# Revit family: 10_給気タイプ 消音形 単相100V_3相200V-60
name_source: partatom
category: 機械設備
units: mm (PartAtom-declared; Revit-internal decimal feet)

## family parameters
OmniClass タイトル = Centrifugal Fans
OmniClass 番号 = 23.75.35.17.27
パーツ タイプ = 割り込み
ロード時にボイドで切り取り = いいえ
丸型コネクタ寸法 = 直径を使用
作業面ベース = いいえ
共有 = いいえ
常に垂直 = はい
部屋計算ポイント = はい

## types (7) — shared parameters
Clearance Left = 450  [stored 1.47638 ft]
IfcExportAs = IfcFanType
IfcExportType = CENTRIFUGALFORWARDCURVED
MID静圧 = 0.0 Pa
MID風量 = 0.0 m³/h
OmniClassCode = 23-33 31 19 13 15
URL = https://www.mitsubishielectric.co.jp
Uniclass2015Code = Pr_65_67_29_12
Uniclass2015Title = Centrifugal fans
Uniclass2015Version = Systems v1.9
サービススペース = はい
ファンの種類 = 多翼形
仕様書バージョン = Version1.0
企業コード = 108420
分類コード = 50052502100020
参照している仕様書等のバージョン = 公共建築工事標準仕様書（機械設備工事編）平成31年度版
周波数 = 60 Hz
呼称 = 消音ボックス付送風機
実風量 = 0.0 m³/h
本体マテリアル = 溶融亜鉛めっき鋼板
極 = 4
法定耐用年数 = 15
盤工事区分 = 電気工事
積算_科目 = 2 換気設備
製品リリース年月 = 2020年4月27日
製品出荷対象 = 国内
製造元 = 三菱電機株式会社
設置方法 = 天吊
説明 = ストレートシロッコファン給気タイプ消音形
負荷分類 = 3_ファン類
運転質量 = 0.00 kg
zero-valued in all types: Clearance Back, Clearance Bottom, Clearance Front, Clearance Right, Clearance Top

## per-type parameters (varying)
- BFS-40SSUA: Depth=378  [stored 1.24016 ft]; Height=255  [stored 0.836614 ft]; M=70  [stored 0.229659 ft]; MAX静圧=97.0 Pa; MAX風量=400.0 m³/h; MIN静圧=41.0 Pa; MIN風量=204.0 m³/h; Width=282; ダクト径=150 mm; 価格=86900 $; 天吊金具ピッチ奥行=343  [stored 1.12533 ft]; 天吊金具ピッチ幅=358  [stored 1.17454 ft]; 形名=BFS-SSUA : BFS-40SSUA; 極数=2; 消費電力=85 W; 番手=#1 1/4; 相=1; 製品質量=10.50 kg; 質量=12.60 kg; 電動機出力=35 W; 電圧=100 V; 騒音レベル(dB(A))=42; 騒音レベル(dB(A))_側面=20.5; 騒音レベル(dB(A))_吐出=39; 騒音レベル(dB(A))_吸込=42
- BFS-50SSUA: Depth=423  [stored 1.3878 ft]; Height=255  [stored 0.836614 ft]; M=85  [stored 0.278871 ft]; MAX静圧=190.0 Pa; MAX風量=500.0 m³/h; MIN静圧=120.0 Pa; MIN風量=395.0 m³/h; Width=325  [stored 1.06627 ft]; ダクト径=200 mm; 価格=123000 $; 天吊金具ピッチ奥行=388  [stored 1.27297 ft]; 天吊金具ピッチ幅=401  [stored 1.31562 ft]; 形名=BFS-SSUA : BFS-50SSUA; 極数=2; 消費電力=100 W; 番手=#1 1/4; 相=1; 製品質量=12.50 kg; 質量=15.00 kg; 電動機出力=45 W; 電圧=100 V; 騒音レベル(dB(A))=45.5; 騒音レベル(dB(A))_側面=23.5; 騒音レベル(dB(A))_吐出=41; 騒音レベル(dB(A))_吸込=45.5
- BFS-80SSUA: Depth=463  [stored 1.51903 ft]; Height=305  [stored 1.00066 ft]; M=85  [stored 0.278871 ft]; MAX静圧=165.0 Pa; MAX風量=800.0 m³/h; MIN静圧=109.0 Pa; MIN風量=650.0 m³/h; Width=373  [stored 1.22375 ft]; ダクト径=200 mm; 価格=137000 $; 天吊金具ピッチ奥行=428  [stored 1.4042 ft]; 天吊金具ピッチ幅=449  [stored 1.4731 ft]; 形名=BFS-SSUA : BFS-80SSUA; 極数=2; 消費電力=210 W; 番手=#1 1/4; 相=1; 製品質量=16.00 kg; 質量=19.20 kg; 電動機出力=110 W; 電圧=100 V; 騒音レベル(dB(A))=51; 騒音レベル(dB(A))_側面=28; 騒音レベル(dB(A))_吐出=44.5; 騒音レベル(dB(A))_吸込=51
- BFS-100SSUA: Depth=488  [stored 1.60105 ft]; Height=305  [stored 1.00066 ft]; M=85  [stored 0.278871 ft]; MAX静圧=260.0 Pa; MAX風量=1000.0 m³/h; MIN静圧=215.0 Pa; MIN風量=880.0 m³/h; Width=393  [stored 1.28937 ft]; ダクト径=200 mm; 価格=154000 $; 天吊金具ピッチ奥行=453  [stored 1.48622 ft]; 天吊金具ピッチ幅=469; 形名=BFS-SSUA : BFS-100SSUA; 極数=2; 消費電力=280 W; 番手=#1 1/2; 相=1; 製品質量=18.00 kg; 質量=21.60 kg; 電動機出力=200 W; 電圧=100 V; 騒音レベル(dB(A))=53; 騒音レベル(dB(A))_側面=32; 騒音レベル(dB(A))_吐出=51; 騒音レベル(dB(A))_吸込=53
- BFS-150SSUA: Depth=590  [stored 1.9357 ft]; Height=350  [stored 1.14829 ft]; M=85  [stored 0.278871 ft]; MAX静圧=320.0 Pa; MAX風量=1500.0 m³/h; MIN静圧=230.0 Pa; MIN風量=1275.0 m³/h; Width=391; ダクト径=250 mm; 価格=176000 $; 天吊金具ピッチ奥行=555  [stored 1.82087 ft]; 天吊金具ピッチ幅=467  [stored 1.53215 ft]; 形名=BFS-SSUA : BFS-150SSUA; 極数=2; 消費電力=515 W; 番手=#1 1/2; 相=1; 製品質量=23.50 kg; 質量=28.20 kg; 電動機出力=300 W; 電圧=100 V; 騒音レベル(dB(A))=60.5; 騒音レベル(dB(A))_側面=35; 騒音レベル(dB(A))_吐出=56; 騒音レベル(dB(A))_吸込=60.5
- BFS-150STUA: Depth=590  [stored 1.9357 ft]; Height=350  [stored 1.14829 ft]; M=85  [stored 0.278871 ft]; MAX静圧=320.0 Pa; MAX風量=1500.0 m³/h; MIN静圧=175.0 Pa; MIN風量=1110.0 m³/h; Width=391; ダクト径=250 mm; 価格=176000 $; 天吊金具ピッチ奥行=555  [stored 1.82087 ft]; 天吊金具ピッチ幅=467  [stored 1.53215 ft]; 形名=BFS-STUA : BFS-150STUA; 極数=3; 消費電力=440 W; 番手=#1 1/2; 相=3; 製品質量=23.50 kg; 質量=28.20 kg; 電動機出力=350 W; 電圧=200 V; 騒音レベル(dB(A))=57.5; 騒音レベル(dB(A))_側面=35; 騒音レベル(dB(A))_吐出=56; 騒音レベル(dB(A))_吸込=57.5
- BFS-210STUA: Depth=645  [stored 2.11614 ft]; Height=350  [stored 1.14829 ft]; M=100  [stored 0.328084 ft]; MAX静圧=325.0 Pa; MAX風量=2100.0 m³/h; MIN静圧=0.0 Pa; MIN風量=0.0 m³/h; Width=476  [stored 1.56168 ft]; ダクト径=300 mm; 価格=271000 $; 天吊金具ピッチ奥行=610  [stored 2.00131 ft]; 天吊金具ピッチ幅=552  [stored 1.81102 ft]; 形名=BFS-STUA : BFS-210STUA; 極数=3; 消費電力=700 W; 番手=#1 1/2; 相=3; 製品質量=26.50 kg; 質量=31.80 kg; 電動機出力=490 W; 電圧=200 V; 騒音レベル(dB(A))=64.5; 騒音レベル(dB(A))_側面=38; 騒音レベル(dB(A))_吐出=59.5; 騒音レベル(dB(A))_吸込=64.5

note: column(s) folded — value = type name in every type: モデル

note: [stored X ft] marks values corroborated as IEEE doubles in the binary element streams (Revit-internal decimal feet)
